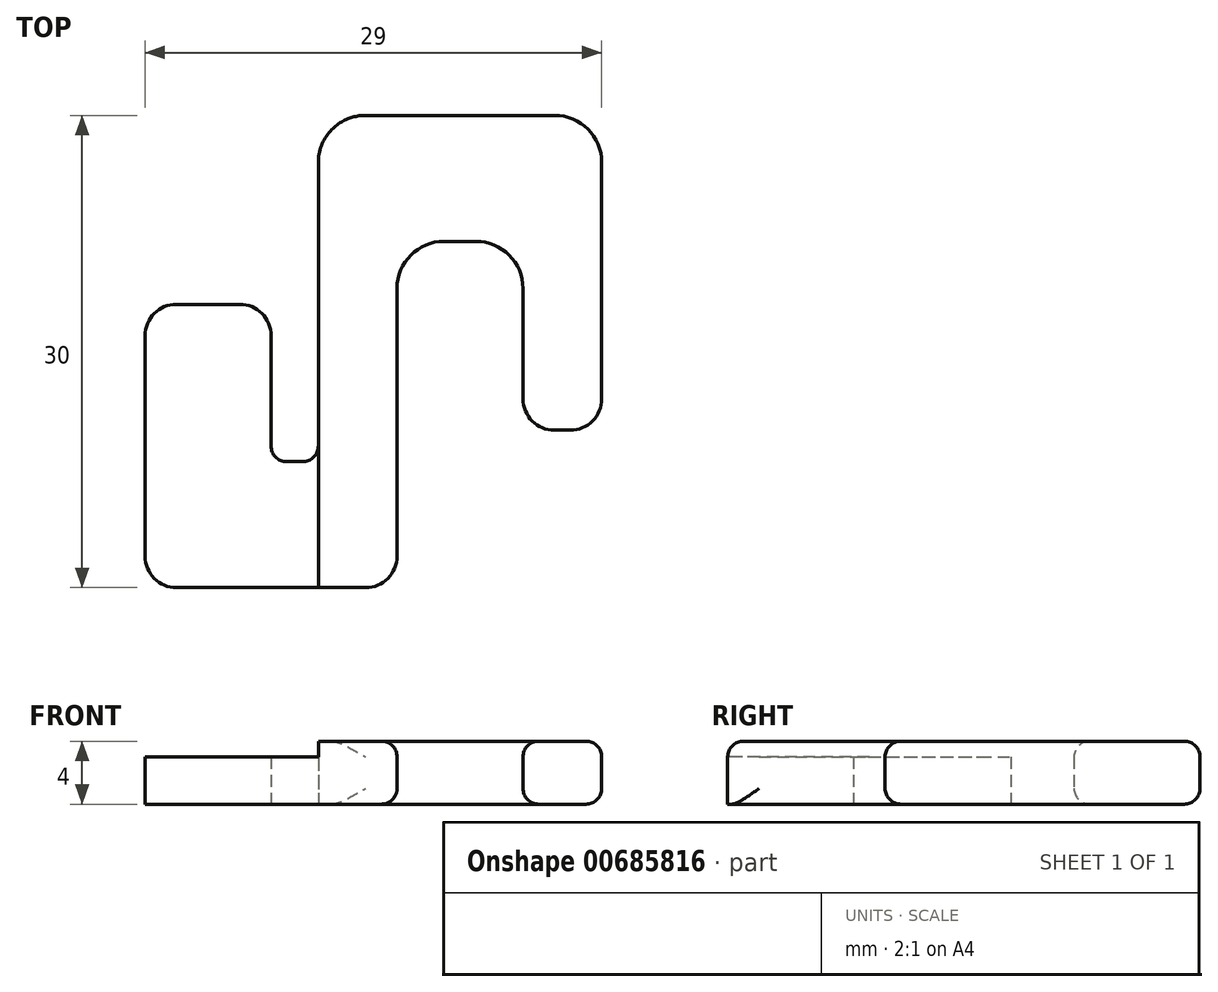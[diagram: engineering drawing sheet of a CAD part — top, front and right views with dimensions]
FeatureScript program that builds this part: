
annotation { "Feature Type Name" : "Feature", "Feature Type Description" : "" }
export const myFeature = defineFeature(function(context is Context, id is Id, definition is map)
    precondition{}
    {
        {
            var Q0;
            Q0=qCreatedBy(makeId("Top.planeOp"),FACE);
            var sketch = newSketch(context, id + "F0", { "sketchPlane" : qUnion([Q0])});
            skLineSegment(sketch, "E0.bottom", {"start": v(2, 0) * mm, "end": v(8, 0) * mm});
            skLineSegment(sketch, "E0.top", {"start": v(2, 18) * mm, "end": v(6, 18) * mm});
            skLineSegment(sketch, "E0.left", {"start": v(0, 2) * mm, "end": v(0, 16) * mm});
            skLineSegment(sketch, "E0.right", {"start": v(8, 9) * mm, "end": v(8, 16) * mm});
            skLineSegment(sketch, "E1.bottom", {"start": v(8, 0) * mm, "end": v(11, 0) * mm});
            skLineSegment(sketch, "E1.top", {"start": v(9, 8) * mm, "end": v(10, 8) * mm});
            skLineSegment(sketch, "E2.bottom", {"start": v(11, 0) * mm, "end": v(14, 0) * mm});
            skLineSegment(sketch, "E2.top", {"start": v(14, 30) * mm, "end": v(16, 30) * mm});
            skLineSegment(sketch, "E2.left", {"start": v(11, 9) * mm, "end": v(11, 27) * mm});
            skLineSegment(sketch, "E2.right", {"start": v(16, 2) * mm, "end": v(16, 19) * mm});
            skLineSegment(sketch, "E3.bottom", {"start": v(16, 30) * mm, "end": v(24, 30) * mm});
            skLineSegment(sketch, "E3.top", {"start": v(19, 22) * mm, "end": v(21, 22) * mm});
            skLineSegment(sketch, "E4.bottom", {"start": v(24, 30) * mm, "end": v(26, 30) * mm});
            skLineSegment(sketch, "E4.top", {"start": v(26, 10) * mm, "end": v(27, 10) * mm});
            skLineSegment(sketch, "E4.left", {"start": v(24, 19) * mm, "end": v(24, 12) * mm});
            skLineSegment(sketch, "E4.right", {"start": v(29, 27) * mm, "end": v(29, 12) * mm});
            skPoint(sketch, "E5.visualSharp", {"position": v(8, 8) * mm});
            skArc(sketch, "E5.filletArc", {"start": v(8, 9) * mm, "mid": v(8.3, 8.3) * mm, "end": v(9, 8) * mm});
            skPoint(sketch, "E6.visualSharp", {"position": v(11, 8) * mm});
            skArc(sketch, "E6.filletArc", {"start": v(10, 8) * mm, "mid": v(10.7, 8.3) * mm, "end": v(11, 9) * mm});
            skPoint(sketch, "E7.visualSharp", {"position": v(16, 22) * mm});
            skArc(sketch, "E7.filletArc", {"start": v(19, 22) * mm, "mid": v(16.88, 21.12) * mm, "end": v(16, 19) * mm});
            skPoint(sketch, "E8.visualSharp", {"position": v(24, 22) * mm});
            skArc(sketch, "E8.filletArc", {"start": v(24, 19) * mm, "mid": v(23.12, 21.12) * mm, "end": v(21, 22) * mm});
            skPoint(sketch, "E9.visualSharp", {"position": v(29, 30) * mm});
            skArc(sketch, "E9.filletArc", {"start": v(29, 27) * mm, "mid": v(28.12, 29.12) * mm, "end": v(26, 30) * mm});
            skPoint(sketch, "E10.visualSharp", {"position": v(11, 30) * mm});
            skArc(sketch, "E10.filletArc", {"start": v(14, 30) * mm, "mid": v(11.88, 29.12) * mm, "end": v(11, 27) * mm});
            skPoint(sketch, "E11.visualSharp", {"position": v(24, 10) * mm});
            skPoint(sketch, "E12.visualSharp", {"position": v(29, 10) * mm});
            skArc(sketch, "E12.filletArc", {"start": v(27, 10) * mm, "mid": v(28.41, 10.59) * mm, "end": v(29, 12) * mm});
            skPoint(sketch, "E13.visualSharp", {"position": v(16, 0) * mm});
            skArc(sketch, "E13.filletArc", {"start": v(14, 0) * mm, "mid": v(15.41, 0.59) * mm, "end": v(16, 2) * mm});
            skPoint(sketch, "E14.visualSharp", {"position": v(8, 18) * mm});
            skArc(sketch, "E14.filletArc", {"start": v(8, 16) * mm, "mid": v(7.41, 17.41) * mm, "end": v(6, 18) * mm});
            skPoint(sketch, "E15.visualSharp", {"position": v(0, 18) * mm});
            skArc(sketch, "E15.filletArc", {"start": v(2, 18) * mm, "mid": v(0.59, 17.41) * mm, "end": v(0, 16) * mm});
            skPoint(sketch, "E16.visualSharp", {"position": v(0, 0) * mm});
            skArc(sketch, "E16.filletArc", {"start": v(0, 2) * mm, "mid": v(0.59, 0.59) * mm, "end": v(2, 0) * mm});
            skArc(sketch, "E17.filletArc", {"start": v(24, 12) * mm, "mid": v(24.59, 10.59) * mm, "end": v(26, 10) * mm});
            skLineSegment(sketch, "E18", {"start": v(11, 9) * mm, "end": v(11, 0) * mm});
            skSolve(sketch);
        }
        {
            var Q0;
            Q0=makeQuery(id+"F0.imprint","IMPRINT",FACE,{"disambiguationData":[TD([[makeQuery(id+"F0.imprint","IMPRINT",EDGE,{"derivedFrom":sQuery(id+"F0.wireOp",EDGE,"E0.bottom")}),1.0]])]});
            extrude(context, id + "F1", {"entities" : qUnion([Q0]), "depth" : 3 * mm, "offsetDistance" : 25 * mm});
        }
        {
            var Q0;
            Q0=makeQuery(id+"F0.imprint","IMPRINT",FACE,{"disambiguationData":[TD([[makeQuery(id+"F0.imprint","IMPRINT",EDGE,{"derivedFrom":sQuery(id+"F0.wireOp",EDGE,"E2.bottom")}),1.0]])]});
            extrude(context, id + "F2", {"entities" : qUnion([Q0]), "operationType" : NewBodyOperationType.ADD, "depth" : 4 * mm, "offsetDistance" : 25 * mm});
        }
        {
            var Q0;
            Q0=makeQuery(id+"F2.opExtrude","CAP_EDGE",EDGE,{"disambiguationData":[OSD([sQuery(id+"F0.wireOp",EDGE,"E4.right")])],"isStart":false});
            var Q1;
            Q1=makeQuery(id+"F2.opExtrude","CAP_EDGE",EDGE,{"disambiguationData":[OSD([sQuery(id+"F0.wireOp",EDGE,"E12.filletArc")])],"isStart":false});
            var Q2;
            Q2=makeQuery(id+"F2.opExtrude","CAP_EDGE",EDGE,{"disambiguationData":[OSD([sQuery(id+"F0.wireOp",EDGE,"E4.top")])],"isStart":false});
            var Q3;
            Q3=makeQuery(id+"F2.opExtrude","CAP_EDGE",EDGE,{"disambiguationData":[OSD([sQuery(id+"F0.wireOp",EDGE,"E17.filletArc")])],"isStart":false});
            var Q4;
            Q4=makeQuery(id+"F2.opExtrude","CAP_EDGE",EDGE,{"disambiguationData":[OSD([sQuery(id+"F0.wireOp",EDGE,"E4.left")])],"isStart":false});
            var Q5;
            Q5=makeQuery(id+"F2.opExtrude","CAP_EDGE",EDGE,{"disambiguationData":[OSD([sQuery(id+"F0.wireOp",EDGE,"E8.filletArc")])],"isStart":false});
            var Q6;
            Q6=makeQuery(id+"F2.opExtrude","CAP_EDGE",EDGE,{"disambiguationData":[OSD([sQuery(id+"F0.wireOp",EDGE,"E3.top")])],"isStart":false});
            var Q7;
            Q7=makeQuery(id+"F2.opExtrude","CAP_EDGE",EDGE,{"disambiguationData":[OSD([sQuery(id+"F0.wireOp",EDGE,"E7.filletArc")])],"isStart":false});
            var Q8;
            Q8=makeQuery(id+"F2.opExtrude","CAP_EDGE",EDGE,{"disambiguationData":[OSD([sQuery(id+"F0.wireOp",EDGE,"E2.right")])],"isStart":false});
            var Q9;
            Q9=makeQuery(id+"F2.opExtrude","CAP_EDGE",EDGE,{"disambiguationData":[OSD([sQuery(id+"F0.wireOp",EDGE,"E13.filletArc")])],"isStart":false});
            var Q10;
            Q10=makeQuery(id+"F2.opExtrude","CAP_EDGE",EDGE,{"disambiguationData":[OSD([sQuery(id+"F0.wireOp",EDGE,"E9.filletArc")])],"isStart":false});
            var Q11;
            Q11=makeQuery(id+"F2.opExtrude","CAP_EDGE",EDGE,{"disambiguationData":[OSD([sQuery(id+"F0.wireOp",EDGE,"E2.top"),sQuery(id+"F0.wireOp",EDGE,"E3.bottom"),sQuery(id+"F0.wireOp",EDGE,"E4.bottom")])],"isStart":false});
            var Q12;
            Q12=makeQuery(id+"F2.opExtrude","CAP_EDGE",EDGE,{"disambiguationData":[OSD([sQuery(id+"F0.wireOp",EDGE,"E7.filletArc")])],"isStart":true});
            var Q13;
            Q13=makeQuery(id+"F2.opExtrude","CAP_EDGE",EDGE,{"disambiguationData":[OSD([sQuery(id+"F0.wireOp",EDGE,"E4.right")])],"isStart":true});
            var Q14;
            Q14=makeQuery(id+"F2.opExtrude","CAP_EDGE",EDGE,{"disambiguationData":[OSD([sQuery(id+"F0.wireOp",EDGE,"E9.filletArc")])],"isStart":true});
            var Q15;
            Q15=makeQuery(id+"F2.opExtrude","CAP_EDGE",EDGE,{"disambiguationData":[OSD([sQuery(id+"F0.wireOp",EDGE,"E2.top"),sQuery(id+"F0.wireOp",EDGE,"E3.bottom"),sQuery(id+"F0.wireOp",EDGE,"E4.bottom")])],"isStart":true});
            var Q16;
            Q16=makeQuery(id+"F2.opExtrude","CAP_EDGE",EDGE,{"disambiguationData":[OSD([sQuery(id+"F0.wireOp",EDGE,"E12.filletArc")])],"isStart":true});
            var Q17;
            Q17=makeQuery(id+"F2.opExtrude","CAP_EDGE",EDGE,{"disambiguationData":[OSD([sQuery(id+"F0.wireOp",EDGE,"E4.top")])],"isStart":true});
            var Q18;
            Q18=makeQuery(id+"F2.opExtrude","CAP_EDGE",EDGE,{"disambiguationData":[OSD([sQuery(id+"F0.wireOp",EDGE,"E17.filletArc")])],"isStart":true});
            var Q19;
            Q19=makeQuery(id+"F2.opExtrude","CAP_EDGE",EDGE,{"disambiguationData":[OSD([sQuery(id+"F0.wireOp",EDGE,"E4.left")])],"isStart":true});
            var Q20;
            Q20=makeQuery(id+"F2.opExtrude","CAP_EDGE",EDGE,{"disambiguationData":[OSD([sQuery(id+"F0.wireOp",EDGE,"E8.filletArc")])],"isStart":true});
            var Q21;
            Q21=makeQuery(id+"F2.opExtrude","CAP_EDGE",EDGE,{"disambiguationData":[OSD([sQuery(id+"F0.wireOp",EDGE,"E3.top")])],"isStart":true});
            var Q22;
            Q22=makeQuery(id+"F2.opExtrude","CAP_EDGE",EDGE,{"disambiguationData":[OSD([sQuery(id+"F0.wireOp",EDGE,"E2.right")])],"isStart":true});
            var Q23;
            Q23=makeQuery(id+"F2.opExtrude","CAP_EDGE",EDGE,{"disambiguationData":[OSD([sQuery(id+"F0.wireOp",EDGE,"E2.bottom")])],"isStart":false});
            fillet(context, id + "F3", {"entities" : qUnion([Q0, Q1, Q2, Q3, Q4, Q5, Q6, Q7, Q8, Q9, Q10, Q11, Q12, Q13, Q14, Q15, Q16, Q17, Q18, Q19, Q20, Q21, Q22, Q23]), "radius" : 1 * mm, "allowEdgeOverflow" : false});
        }
    });
